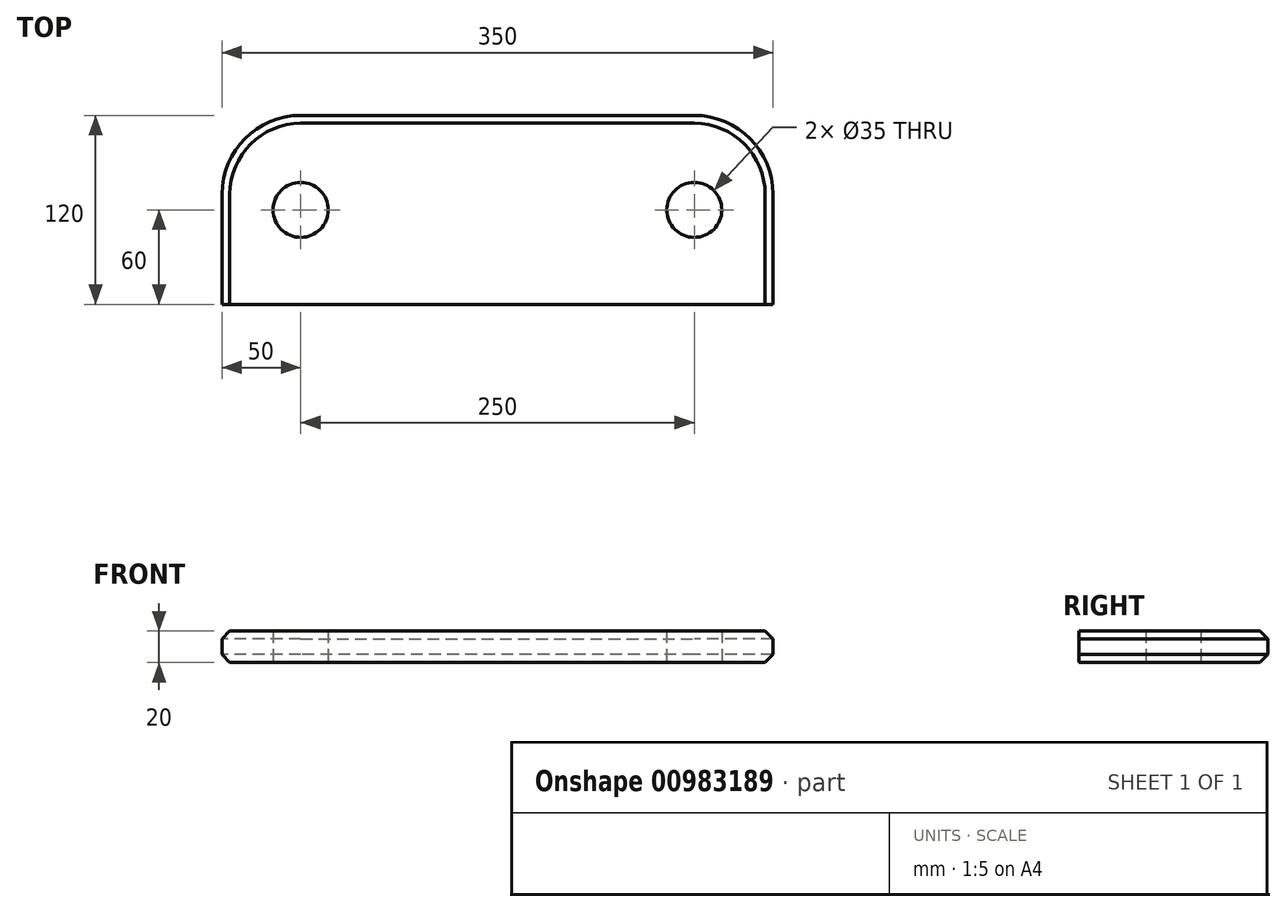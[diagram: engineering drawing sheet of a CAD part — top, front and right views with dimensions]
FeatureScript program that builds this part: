
annotation { "Feature Type Name" : "Feature", "Feature Type Description" : "" }
export const myFeature = defineFeature(function(context is Context, id is Id, definition is map)
    precondition{}
    {
        {
            var Q0;
            Q0=qCreatedBy(makeId("Top.planeOp"),FACE);
            var sketch = newSketch(context, id + "F0", { "sketchPlane" : qUnion([Q0])});
            skLineSegment(sketch, "E0.bottom", {"start": v(175, -60) * mm, "end": v(-175, -60) * mm});
            skLineSegment(sketch, "E0.top", {"start": v(175, 60) * mm, "end": v(-175, 60) * mm});
            skLineSegment(sketch, "E0.left", {"start": v(175, -60) * mm, "end": v(175, 60) * mm});
            skLineSegment(sketch, "E0.right", {"start": v(-175, -60) * mm, "end": v(-175, 60) * mm});
            skPoint(sketch, "E0.middle", {"position": v(0, 0) * mm});
            skCircle(sketch, "E1", {"center": v(-125, 0) * mm, "radius": 17.5 * mm});
            skCircle(sketch, "E2", {"center": v(125, 0) * mm, "radius": 17.5 * mm});
            skSolve(sketch);
        }
        {
            var Q0;
            Q0 = qSketchRegion(id + "F0", true);
            extrude(context, id + "F1", {"entities" : qUnion([Q0]), "depth" : 20 * mm, "offsetDistance" : 25 * mm});
        }
        {
            var Q0;
            Q0=makeQuery(id+"F1.opExtrude","SWEPT_EDGE",EDGE,{"disambiguationData":[OSD([sQuery(id+"F0.wireOp",EDGE,"E0.top"),sQuery(id+"F0.wireOp",EDGE,"E0.left")])]});
            var Q1;
            Q1=makeQuery(id+"F1.opExtrude","SWEPT_EDGE",EDGE,{"disambiguationData":[OSD([sQuery(id+"F0.wireOp",EDGE,"E0.top"),sQuery(id+"F0.wireOp",EDGE,"E0.right")])]});
            fillet(context, id + "F2", {"entities" : qUnion([Q0, Q1]), "tangentPropagation" : true, "radius" : 50 * mm, "defaultsChanged" : false, "vertexSettings" : [], "allowEdgeOverflow" : false});
        }
        {
            var Q0;
            Q0=makeQuery(id+"F1.opExtrude","CAP_EDGE",EDGE,{"disambiguationData":[OSD([sQuery(id+"F0.wireOp",EDGE,"E0.left")])],"isStart":true});
            var Q1;
            Q1=makeQuery(id+"F1.opExtrude","CAP_EDGE",EDGE,{"disambiguationData":[OSD([sQuery(id+"F0.wireOp",EDGE,"E0.top")])],"isStart":false});
            chamfer(context, id + "F3", {"entities" : qUnion([Q0, Q1]), "width" : 5 * mm, "tangentPropagation" : true});
        }
    });
